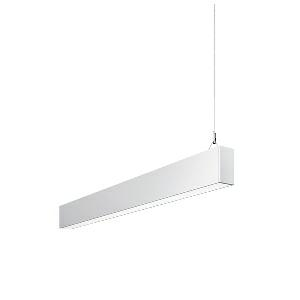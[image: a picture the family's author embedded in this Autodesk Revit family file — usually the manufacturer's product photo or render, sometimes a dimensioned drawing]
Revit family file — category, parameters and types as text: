
# Revit family: dotoo_line_-_dlp_1500_830_d_end_00805804_f3b2
name_source: partatom
category: Lighting Fixtures
units: mm (PartAtom-declared; Revit-internal decimal feet)

## family parameters
Cut with Voids When Loaded = No
Host = Face
Light Source = No
Part Type = Normal
Room Calculation Point = No
Round Connector Dimension = Use Diameter
Shared = No

## types (1)
- DOTOO.line - DLP 1500/830/D END (1 x LED, 1300 lm, 3000K)
    Apparent Load = 13 VA
    Approval mark = CE
    CIE Flux Codes = 67 91 98 100 100
    Color Rendering = 80-89
    Color Temperature = 3000K
    Control Gear = Electronic ballast
    Default Elevation = 1800 mm
    Description = DLP 1500/830/D|Suspended luminaire|light source: LED|connected load: 220-240 V, 50/60 Hz|Power consumption: approx. 13 W|standby: approx. 0,20|luminous flux: 1300 lm|luminous efficacy: 100 lm/W|light distribution: Direct|direct ratio: approx. 100 %|colour temperature: Warm white, ca. 3000 K|color rendering index (CRI): >= 80|chromaticity tolerance:  3 SDCM|System of protection: IP 40|technology: Continuously dimmable|luminaire body|material: Sectional aluminium|colour: White|lamp cover: Acrylic (PMMA), Clear|mains lead: 1,0 m With free stranded wires|Fastening: Steel cable 0.3 - 0.7 m|glare control: Prism aperture|luminance(L65): <= 3000 cd/m|unified glare rating(4H 8H): <=  19|special features: DALI Load 1x, TouchDIM - dimming via standard switch, Through-wired, up to 18 m on one mains connection, Flicker-free, Suitable as emergency lighting, Mechanical and electrical connection of the individual modules without tools|
    Frequency = 50 Hz
    Height = 110 mm
    Lamp = 1 x LED
    Lamp Light Flux = 1300 lm
    Lamp count = 1
    Length = 1128 mm
    Luminous efficacy = 100 lm/W
    Manufacturer = Waldmann
    ModVariant = No
    Model = 00805804
    Mounting Place = Ceiling
    Mounting Type = Pendant
    Number of Poles = 1
    OnlyDefault = Yes
    Power Factor = 1
    Product Name = DOTOO.line - DLP 1500/830/D END
    Product group = Suspended luminaire
    ProductGroupID = 9
    Protection Class = Protection class I
    Protection Degree = IP 40
    RLX_Detail_Level = 1
    RLX_Emergency_Light_Flux = 0 lm
    RLX_Emergency_Type = 0
    RLX_Emergency_Type_DB = No
    RlxData = <blob elided: 18297 chars, md5=3559cd70>
    Socket = socket
    Standby Power = 0 W
    System Light Flux = 1300 lm
    System Power = 13 W
    Type Comments = Product without accessories
    Type Image = 113303000-00692573.jpg
    URL = http://relux.com
    VarID = ---
    Voltage = 230 V
    Voltage Range = 220-240 V
    Weight = 0.00 kg
    Width = 60 mm  [stored 0.19685 ft]

note: [stored X ft] marks values corroborated as IEEE doubles in the binary element streams (Revit-internal decimal feet)

## geometry (parser evidence)
native form markers: Blend x4, Sweep x10
no freeform markers — native parametric forms only
